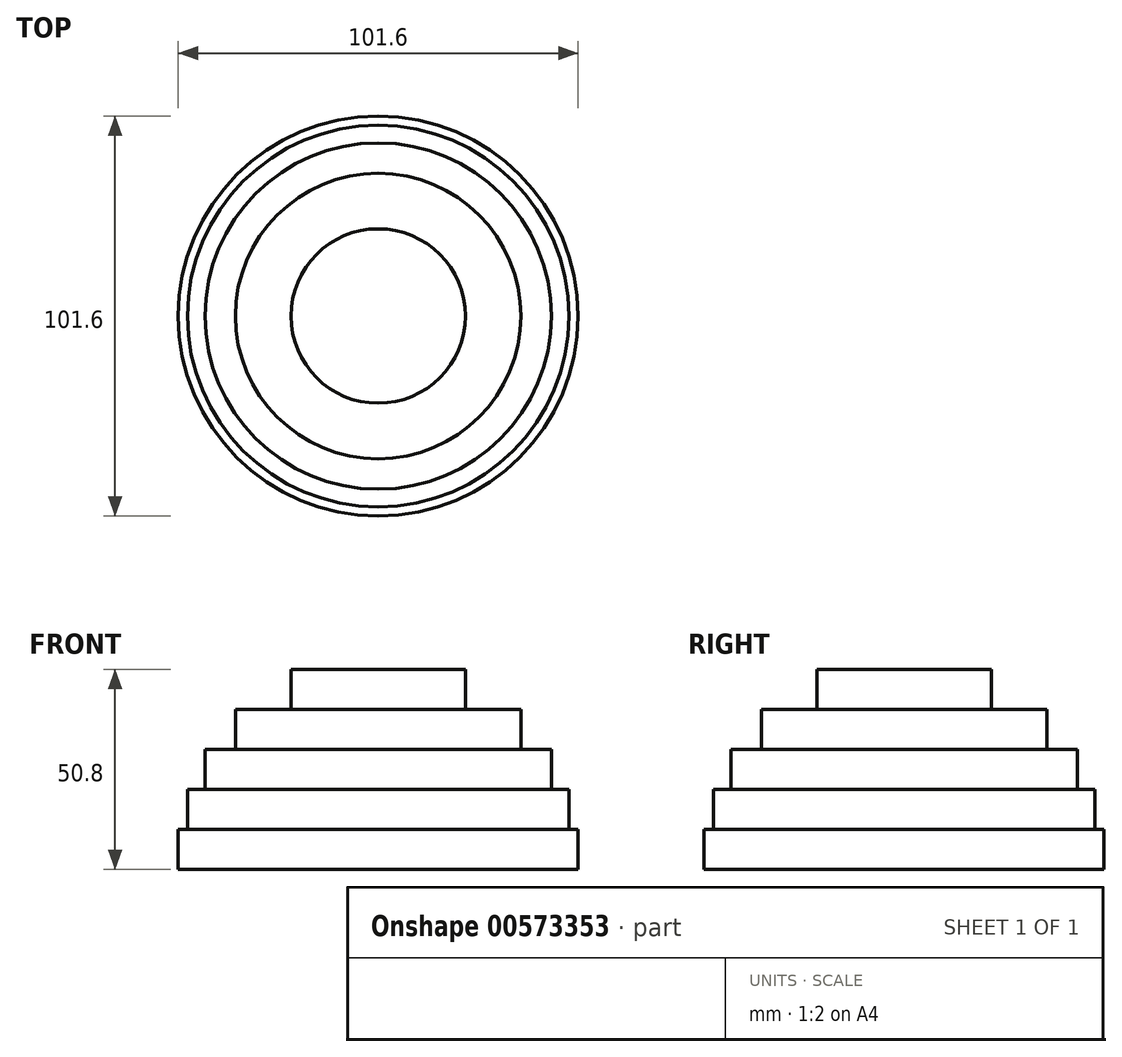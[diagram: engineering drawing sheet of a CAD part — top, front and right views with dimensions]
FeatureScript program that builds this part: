
annotation { "Feature Type Name" : "Feature", "Feature Type Description" : "" }
export const myFeature = defineFeature(function(context is Context, id is Id, definition is map)
    precondition{}
    {
        {
            var Q0;
            Q0=qCreatedBy(makeId("Top.planeOp"),FACE);
            var sketch = newSketch(context, id + "F0", { "sketchPlane" : qUnion([Q0])});
            skCircle(sketch, "E0", {"center": v(0, 0) * mm, "radius": 50.8 * mm});
            skSolve(sketch);
        }
        {
            var Q0;
            Q0 = qSketchRegion(id + "F0", true);
            extrude(context, id + "F1", {"entities" : qUnion([Q0]), "depth" : 10.16 * mm, "offsetDistance" : 25.4 * mm});
        }
        {
            var Q0;
            Q0=makeQuery(id+"F1.opExtrude","CAP_FACE",FACE,{"disambiguationData":[OSD([sQuery(id+"F0.wireOp",EDGE,"E0")])],"isStart":false});
            var sketch = newSketch(context, id + "F2", { "sketchPlane" : qUnion([Q0])});
            skCircle(sketch, "E1", {"center": v(0, 0) * mm, "radius": 48.46 * mm});
            skSolve(sketch);
        }
        {
            var Q0;
            Q0=makeQuery(id+"F2.imprint","IMPRINT",FACE,{"disambiguationData":[TD([[makeQuery(id+"F2.imprint","IMPRINT",EDGE,{"derivedFrom":sQuery(id+"F2.wireOp",EDGE,"E1")}),1.0]])]});
            extrude(context, id + "F3", {"entities" : qUnion([Q0]), "operationType" : NewBodyOperationType.ADD, "depth" : 10.16 * mm, "offsetDistance" : 25.4 * mm});
        }
        {
            var Q0;
            Q0=makeQuery(id+"F3.opExtrude","CAP_FACE",FACE,{"disambiguationData":[OSD([sQuery(id+"F2.wireOp",EDGE,"E1")])],"isStart":false});
            var sketch = newSketch(context, id + "F4", { "sketchPlane" : qUnion([Q0])});
            skCircle(sketch, "E2", {"center": v(0, 0) * mm, "radius": 44 * mm});
            skSolve(sketch);
        }
        {
            var Q0;
            Q0=makeQuery(id+"F4.imprint","IMPRINT",FACE,{"disambiguationData":[TD([[makeQuery(id+"F4.imprint","IMPRINT",EDGE,{"derivedFrom":sQuery(id+"F4.wireOp",EDGE,"E2")}),1.0]])]});
            extrude(context, id + "F5", {"entities" : qUnion([Q0]), "operationType" : NewBodyOperationType.ADD, "depth" : 10.16 * mm, "offsetDistance" : 25.4 * mm});
        }
        {
            var Q0;
            Q0=makeQuery(id+"F5.opExtrude","CAP_FACE",FACE,{"disambiguationData":[OSD([sQuery(id+"F4.wireOp",EDGE,"E2")])],"isStart":false});
            var sketch = newSketch(context, id + "F6", { "sketchPlane" : qUnion([Q0])});
            skCircle(sketch, "E3", {"center": v(0, 0) * mm, "radius": 36.27 * mm});
            skSolve(sketch);
        }
        {
            var Q0;
            Q0=makeQuery(id+"F6.imprint","IMPRINT",FACE,{"disambiguationData":[TD([[makeQuery(id+"F6.imprint","IMPRINT",EDGE,{"derivedFrom":sQuery(id+"F6.wireOp",EDGE,"E3")}),1.0]])]});
            extrude(context, id + "F7", {"entities" : qUnion([Q0]), "operationType" : NewBodyOperationType.ADD, "depth" : 10.16 * mm, "offsetDistance" : 25.4 * mm});
        }
        {
            var Q0;
            Q0=makeQuery(id+"F7.opExtrude","CAP_FACE",FACE,{"disambiguationData":[OSD([sQuery(id+"F6.wireOp",EDGE,"E3")])],"isStart":false});
            var sketch = newSketch(context, id + "F8", { "sketchPlane" : qUnion([Q0])});
            skCircle(sketch, "E4", {"center": v(0, 0) * mm, "radius": 22.15 * mm});
            skSolve(sketch);
        }
        {
            var Q0;
            Q0=makeQuery(id+"F8.imprint","IMPRINT",FACE,{"disambiguationData":[TD([[makeQuery(id+"F8.imprint","IMPRINT",EDGE,{"derivedFrom":sQuery(id+"F8.wireOp",EDGE,"E4")}),1.0]])]});
            extrude(context, id + "F9", {"entities" : qUnion([Q0]), "operationType" : NewBodyOperationType.ADD, "depth" : 10.16 * mm, "offsetDistance" : 25.4 * mm});
        }
    });
